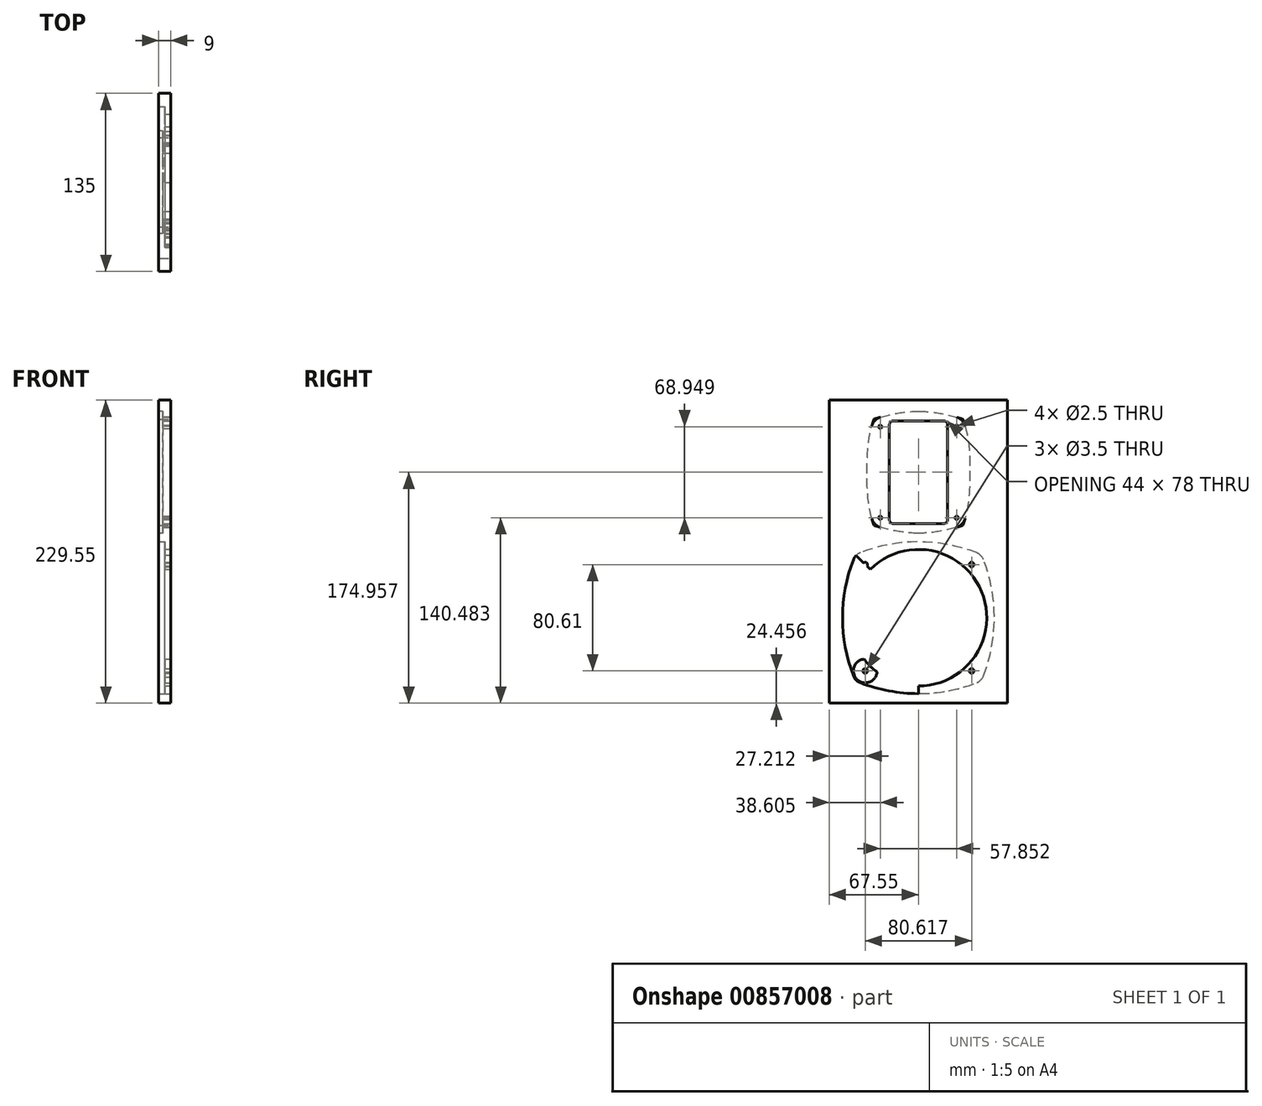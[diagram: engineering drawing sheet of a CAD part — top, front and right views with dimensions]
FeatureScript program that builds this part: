
annotation { "Feature Type Name" : "Feature", "Feature Type Description" : "" }
export const myFeature = defineFeature(function(context is Context, id is Id, definition is map)
    precondition{}
    {
        {
            var Q0;
            Q0=qCreatedBy(makeId("Right.planeOp"),FACE);
            var sketch = newSketch(context, id + "F0", { "sketchPlane" : qUnion([Q0])});
            skLineSegment(sketch, "E0", {"start": v(-66.83, 98.89) * mm, "end": v(-66.83, -130.66) * mm});
            skLineSegment(sketch, "E1", {"start": v(68.17, 98.89) * mm, "end": v(68.17, -130.44) * mm});
            skLineSegment(sketch, "E2", {"start": v(-66.83, 98.89) * mm, "end": v(68.17, 98.89) * mm});
            skLineSegment(sketch, "E3", {"start": v(-66.83, -130.66) * mm, "end": v(68.17, -130.44) * mm});
            skCircle(sketch, "E4", {"center": v(29.63, 78.77) * mm, "radius": 1.25 * mm});
            skPoint(sketch, "E5.orphan", {"position": v(0.7, 83.22) * mm});
            skCircle(sketch, "E6", {"center": v(29.63, 9.82) * mm, "radius": 1.25 * mm});
            skPoint(sketch, "E7", {"position": v(-28.23, 78.77) * mm});
            skPoint(sketch, "E8", {"position": v(-28.23, 9.82) * mm});
            skCircle(sketch, "E9", {"center": v(-28.23, 78.77) * mm, "radius": 1.25 * mm});
            skCircle(sketch, "E10", {"center": v(-28.23, 9.82) * mm, "radius": 1.25 * mm});
            skFitSpline(sketch, "E11", {"points": [v(-33.05, 84.51) * mm, v(0.7, 90.52) * mm, v(34.45, 84.51) * mm], "startDerivative": vector(67.5, 21.85) * mm, "endDerivative": vector(67.5, -21.85) * mm});
            skFitSpline(sketch, "E12", {"points": [v(34.45, 84.51) * mm, v(39.67, 45.72) * mm, v(34.45, 4.08) * mm], "startDerivative": vector(28.29, -80.43) * mm, "endDerivative": vector(-28.29, -80.43) * mm});
            skFitSpline(sketch, "E13", {"points": [v(34.45, 4.08) * mm, v(0.7, -1.9) * mm, v(-33.05, 4.08) * mm], "startDerivative": vector(-67.5, -21.85) * mm, "endDerivative": vector(-67.5, 21.85) * mm});
            skFitSpline(sketch, "E14", {"points": [v(-33.05, 4.08) * mm, v(-38.29, 45.17) * mm, v(-33.05, 84.51) * mm], "startDerivative": vector(-28.18, 80.43) * mm, "endDerivative": vector(28.18, 80.43) * mm});
            skPoint(sketch, "E15.orphan", {"position": v(32.84, 82.6) * mm});
            skPoint(sketch, "E16.orphan", {"position": v(-31.44, 82.6) * mm});
            skArc(sketch, "E17.filletArc", {"start": v(-28.13, 86.02) * mm, "mid": v(-32.24, 83.58) * mm, "end": v(-34.63, 79.45) * mm});
            skArc(sketch, "E18.filletArc", {"start": v(36.04, 79.45) * mm, "mid": v(33.64, 83.58) * mm, "end": v(29.52, 86.02) * mm});
            skPoint(sketch, "E19.orphan", {"position": v(-31.44, 6) * mm});
            skArc(sketch, "E20.filletArc", {"start": v(-34.68, 9.36) * mm, "mid": v(-32.2, 5.05) * mm, "end": v(-27.93, 2.52) * mm});
            skArc(sketch, "E21.filletArc", {"start": v(29.34, 2.52) * mm, "mid": v(33.6, 5.05) * mm, "end": v(36.09, 9.36) * mm});
            skPoint(sketch, "E22.orphan", {"position": v(0.72, 44.3) * mm});
            skLineSegment(sketch, "E23.bottom", {"start": v(19.72, 83.3) * mm, "end": v(-18.28, 83.3) * mm});
            skLineSegment(sketch, "E23.top", {"start": v(19.72, 5.3) * mm, "end": v(-18.28, 5.3) * mm});
            skLineSegment(sketch, "E23.left", {"start": v(22.72, 80.3) * mm, "end": v(22.72, 8.3) * mm});
            skLineSegment(sketch, "E23.right", {"start": v(-21.28, 80.3) * mm, "end": v(-21.28, 8.3) * mm});
            skPoint(sketch, "E24.visualSharp", {"position": v(22.72, 83.3) * mm});
            skArc(sketch, "E24.filletArc", {"start": v(22.72, 80.3) * mm, "mid": v(21.84, 82.42) * mm, "end": v(19.72, 83.3) * mm});
            skPoint(sketch, "E25.visualSharp", {"position": v(-21.28, 83.3) * mm});
            skArc(sketch, "E25.filletArc", {"start": v(-18.28, 83.3) * mm, "mid": v(-20.4, 82.42) * mm, "end": v(-21.28, 80.3) * mm});
            skPoint(sketch, "E26.visualSharp", {"position": v(-21.28, 5.3) * mm});
            skArc(sketch, "E26.filletArc", {"start": v(-21.28, 8.3) * mm, "mid": v(-20.4, 6.18) * mm, "end": v(-18.28, 5.3) * mm});
            skPoint(sketch, "E27.visualSharp", {"position": v(22.72, 5.3) * mm});
            skArc(sketch, "E27.filletArc", {"start": v(19.72, 5.3) * mm, "mid": v(21.84, 6.18) * mm, "end": v(22.72, 8.3) * mm});
            skLineSegment(sketch, "E28", {"start": v(0.72, 44.3) * mm, "end": v(0.7, -130.55) * mm});
            skPoint(sketch, "E29", {"position": v(0.71, -65.9) * mm});
            skLineSegment(sketch, "E30", {"start": v(0.71, -65.9) * mm, "end": v(-45.95, -19.22) * mm});
            skPoint(sketch, "E31", {"position": v(-39.6, -25.59) * mm});
            skCircle(sketch, "E32", {"center": v(-39.6, -25.59) * mm, "radius": 1.75 * mm});
            skLineSegment(sketch, "E33.trimOffspring", {"start": v(-45.95, -19.22) * mm, "end": v(-45.95, -19.22) * mm});
            skPoint(sketch, "E34", {"position": v(0.72, -8.4) * mm});
            skPoint(sketch, "E35", {"position": v(-56.79, -65.9) * mm});
            skCircle(sketch, "E36.1.0", {"center": v(-39.62, -106.2) * mm, "radius": 1.75 * mm});
            skLineSegment(sketch, "E36.1.2", {"start": v(0.73, -65.87) * mm, "end": v(-45.94, -112.54) * mm});
            skCircle(sketch, "E36.2.0", {"center": v(41, -106.2) * mm, "radius": 1.75 * mm});
            skLineSegment(sketch, "E36.2.2", {"start": v(0.76, -65.85) * mm, "end": v(47.42, -112.52) * mm});
            skCircle(sketch, "E36.3.0", {"center": v(41, -25.6) * mm, "radius": 1.75 * mm});
            skPoint(sketch, "E37.2.0", {"position": v(0.7, -123.4) * mm});
            skPoint(sketch, "E37.3.0", {"position": v(58.21, -65.9) * mm});
            skArc(sketch, "E38.3.0", {"start": v(47.42, -112.52) * mm, "mid": v(48.18, -111.66) * mm, "end": v(48.83, -110.7) * mm});
            skArc(sketch, "E39.trimOffspring", {"start": v(-12.32, -130.57) * mm, "mid": v(0.84, -131.87) * mm, "end": v(14, -130.53) * mm});
            skFitSpline(sketch, "E40", {"points": [v(-47.41, -110.7) * mm, v(-56.79, -65.9) * mm, v(-47.4, -21.09) * mm], "startDerivative": vector(-28.2, 89.61) * mm, "endDerivative": vector(28.2, 89.6) * mm});
            skLineSegment(sketch, "E41", {"start": v(0.71, -65.9) * mm, "end": v(48.44, -18.17) * mm});
            skPoint(sketch, "E42", {"position": v(47.38, -19.23) * mm});
            skPoint(sketch, "E43.orphan", {"position": v(-44.1, -114.01) * mm});
            skPoint(sketch, "E44.orphan", {"position": v(45.56, -113.95) * mm});
            skLineSegment(sketch, "E45", {"start": v(0.71, -65.9) * mm, "end": v(-47.02, -18.16) * mm});
            skArc(sketch, "E46", {"start": v(48.44, -18.17) * mm, "mid": v(0.72, -8.4) * mm, "end": v(-47.02, -18.16) * mm});
            skArc(sketch, "E47.1.0", {"start": v(48.44, -113.63) * mm, "mid": v(58.21, -65.9) * mm, "end": v(48.44, -18.17) * mm});
            skArc(sketch, "E47.2.0", {"start": v(-47.02, -113.62) * mm, "mid": v(0.7, -123.4) * mm, "end": v(48.44, -113.63) * mm});
            skLineSegment(sketch, "E47.anchor1", {"start": v(0.71, -65.9) * mm, "end": v(0.7, -129.87) * mm, "construction": true});
            skLineSegment(sketch, "E47.anchor2", {"start": v(0.71, -65.9) * mm, "end": v(0.72, -1.93) * mm, "construction": true});
            skArc(sketch, "E48", {"start": v(-47.02, -18.16) * mm, "mid": v(-56.79, -65.9) * mm, "end": v(-47.02, -113.62) * mm});
            skCircle(sketch, "E49", {"center": v(0.71, -65.9) * mm, "radius": 51.75 * mm});
            skCircle(sketch, "E50", {"center": v(41, -106.2) * mm, "radius": 9 * mm});
            skCircle(sketch, "E51", {"center": v(-39.62, -106.2) * mm, "radius": 9 * mm});
            skLineSegment(sketch, "E52", {"start": v(0.72, 44.3) * mm, "end": v(0.71, 90.52) * mm});
            skPoint(sketch, "E52.endSnap0", {"position": v(0.72, 83.3) * mm});
            skLineSegment(sketch, "E53", {"start": v(29.63, 78.77) * mm, "end": v(-28.23, 78.77) * mm});
            skLineSegment(sketch, "E54", {"start": v(0.72, 44.3) * mm, "end": v(39.24, -1.98) * mm});
            skLineSegment(sketch, "E55", {"start": v(0.72, 44.3) * mm, "end": v(-37.3, -1.39) * mm});
            skSolve(sketch);
        }
        {
            var Q0;
            {var subQ18=sQuery(id+"F0.wireOp",EDGE,"E0");Q0=makeQuery(id+"F0.imprint","IMPRINT",FACE,{"disambiguationData":[TD([[makeQuery(id+"F0.imprint","IMPRINT",EDGE,{"derivedFrom":subQ18}),1.0]])]});}
            var Q1;
            {var subQ11=sQuery(id+"F0.wireOp",EDGE,"E1");Q1=makeQuery(id+"F0.imprint","IMPRINT",FACE,{"disambiguationData":[TD([[makeQuery(id+"F0.imprint","IMPRINT",EDGE,{"derivedFrom":subQ11}),-1.0]])]});}
            extrude(context, id + "F1", {"entities" : qUnion([Q0, Q1]), "oppositeDirection" : true, "depth" : 9 * mm, "offsetDistance" : 25 * mm});
        }
        {
            var Q0;
            Q0=makeQuery(id+"F1.opExtrude","SWEPT_EDGE",EDGE,{"disambiguationData":[OSD([sQuery(id+"F0.wireOp",EDGE,"E41"),sQuery(id+"F0.wireOp",EDGE,"E46"),sQuery(id+"F0.wireOp",EDGE,"E47.1.0")])]});
            var Q1;
            Q1=makeQuery(id+"F1.opExtrude","SWEPT_EDGE",EDGE,{"disambiguationData":[OSD([sQuery(id+"F0.wireOp",EDGE,"E45"),sQuery(id+"F0.wireOp",EDGE,"E46"),sQuery(id+"F0.wireOp",EDGE,"E48")])]});
            var Q2;
            Q2=makeQuery(id+"F1.opExtrude","SWEPT_EDGE",EDGE,{"disambiguationData":[OSD([sQuery(id+"F0.wireOp",EDGE,"E47.1.0"),sQuery(id+"F0.wireOp",EDGE,"E47.2.0")])]});
            var Q3;
            Q3=makeQuery(id+"F1.opExtrude","SWEPT_EDGE",EDGE,{"disambiguationData":[OSD([sQuery(id+"F0.wireOp",EDGE,"E47.2.0"),sQuery(id+"F0.wireOp",EDGE,"E48")])]});
            fillet(context, id + "F2", {"entities" : qUnion([Q0, Q1, Q2, Q3]), "radius" : 9 * mm, "allowEdgeOverflow" : false});
        }
        {
            var Q0;
            {var subQ14=sQuery(id+"F0.wireOp",EDGE,"E47.1.0");Q0=makeQuery(id+"F0.imprint","IMPRINT",FACE,{"disambiguationData":[TD([[makeQuery(id+"F0.imprint","IMPRINT",EDGE,{"derivedFrom":subQ14}),1.0]])]});}
            var Q1;
            {var subQ0=sQuery(id+"F0.wireOp",EDGE,"E46");var subQ8=sQuery(id+"F0.wireOp",EDGE,"E28");var subQ9=makeQuery(id+"F0.imprint","INTERSECT",VERTEX,{"derivedFrom":[subQ8,subQ0]});Q1=makeQuery(id+"F0.imprint","IMPRINT",FACE,{"disambiguationData":[TD([[makeQuery(id+"F0.imprint","IMPRINT",EDGE,{"disambiguationData":[TD([[subQ9,-1.0]])],"derivedFrom":subQ8}),1.0]])]});}
            var Q2;
            {var subQ0=sQuery(id+"F0.wireOp",EDGE,"E45");var subQ10=makeQuery(id+"F0.imprint","IMPRINT",VERTEX,{"derivedFrom":subQ0});Q2=makeQuery(id+"F0.imprint","IMPRINT",FACE,{"disambiguationData":[TD([[makeQuery(id+"F0.imprint","IMPRINT",EDGE,{"disambiguationData":[TD([[subQ10,1.0]])],"derivedFrom":subQ0}),-1.0]])]});}
            var Q3;
            {var subQ0=sQuery(id+"F0.wireOp",EDGE,"E48");var subQ1=makeQuery(id+"F0.imprint","IMPRINT",VERTEX,{"disambiguationData":[OD(0.0)],"derivedFrom":subQ0});Q3=makeQuery(id+"F0.imprint","IMPRINT",FACE,{"disambiguationData":[TD([[makeQuery(id+"F0.imprint","IMPRINT",EDGE,{"disambiguationData":[TD([[subQ1,-1.0]])],"derivedFrom":subQ0}),1.0]])]});}
            var Q4;
            {var subQ1=sQuery(id+"F0.wireOp",EDGE,"E36.2.2");var subQ5=sQuery(id+"F0.wireOp",EDGE,"E36.2.0");var subQ6=makeQuery(id+"F0.imprint","INTERSECT",VERTEX,{"disambiguationData":[OD(0.0)],"derivedFrom":[subQ5,subQ1]});Q4=makeQuery(id+"F0.imprint","IMPRINT",FACE,{"disambiguationData":[TD([[makeQuery(id+"F0.imprint","IMPRINT",EDGE,{"disambiguationData":[TD([[subQ6,1.0]])],"derivedFrom":subQ5}),-1.0]])]});}
            var Q5;
            {var subQ1=sQuery(id+"F0.wireOp",EDGE,"E36.2.2");var subQ5=sQuery(id+"F0.wireOp",EDGE,"E36.2.0");var subQ6=makeQuery(id+"F0.imprint","INTERSECT",VERTEX,{"disambiguationData":[OD(0.0)],"derivedFrom":[subQ5,subQ1]});Q5=makeQuery(id+"F0.imprint","IMPRINT",FACE,{"disambiguationData":[TD([[makeQuery(id+"F0.imprint","IMPRINT",EDGE,{"disambiguationData":[TD([[subQ6,-1.0]])],"derivedFrom":subQ5}),-1.0]])]});}
            var Q6;
            {var subQ1=sQuery(id+"F0.wireOp",EDGE,"E36.1.2");var subQ6=sQuery(id+"F0.wireOp",EDGE,"E36.1.0");var subQ8=makeQuery(id+"F0.imprint","INTERSECT",VERTEX,{"disambiguationData":[OD(0.0)],"derivedFrom":[subQ6,subQ1]});Q6=makeQuery(id+"F0.imprint","IMPRINT",FACE,{"disambiguationData":[TD([[makeQuery(id+"F0.imprint","IMPRINT",EDGE,{"disambiguationData":[TD([[subQ8,1.0]])],"derivedFrom":subQ6}),-1.0]])]});}
            var Q7;
            {var subQ1=sQuery(id+"F0.wireOp",EDGE,"E36.1.2");var subQ5=sQuery(id+"F0.wireOp",EDGE,"E36.1.0");var subQ6=makeQuery(id+"F0.imprint","INTERSECT",VERTEX,{"disambiguationData":[OD(0.0)],"derivedFrom":[subQ5,subQ1]});Q7=makeQuery(id+"F0.imprint","IMPRINT",FACE,{"disambiguationData":[TD([[makeQuery(id+"F0.imprint","IMPRINT",EDGE,{"disambiguationData":[TD([[subQ6,-1.0]])],"derivedFrom":subQ5}),-1.0]])]});}
            extrude(context, id + "F3", {"entities" : qUnion([Q0, Q1, Q2, Q3, Q4, Q5, Q6, Q7]), "operationType" : NewBodyOperationType.ADD, "oppositeDirection" : true, "depth" : 4.5 * mm, "offsetDistance" : 25 * mm});
        }
        {
            var Q0;
            Q0=makeQuery(id+"F0.imprint","IMPRINT",FACE,{"disambiguationData":[TD([[makeQuery(id+"F0.imprint","IMPRINT",EDGE,{"derivedFrom":sQuery(id+"F0.wireOp",EDGE,"E4")}),-1.0]])]});
            var Q1;
            Q1=makeQuery(id+"F0.imprint","IMPRINT",FACE,{"disambiguationData":[TD([[makeQuery(id+"F0.imprint","IMPRINT",EDGE,{"derivedFrom":sQuery(id+"F0.wireOp",EDGE,"E9")}),-1.0]])]});
            var Q2;
            {var subQ0=sQuery(id+"F0.wireOp",EDGE,"E27.filletArc");Q2=makeQuery(id+"F0.imprint","IMPRINT",FACE,{"disambiguationData":[TD([[makeQuery(id+"F0.imprint","IMPRINT",EDGE,{"derivedFrom":subQ0}),-1.0]])]});}
            var Q3;
            {var subQ0=sQuery(id+"F0.wireOp",EDGE,"E26.filletArc");Q3=makeQuery(id+"F0.imprint","IMPRINT",FACE,{"disambiguationData":[TD([[makeQuery(id+"F0.imprint","IMPRINT",EDGE,{"derivedFrom":subQ0}),-1.0]])]});}
            extrude(context, id + "F4", {"entities" : qUnion([Q0, Q1, Q2, Q3]), "operationType" : NewBodyOperationType.ADD, "oppositeDirection" : true, "depth" : 6 * mm, "offsetDistance" : 25 * mm});
        }
    });
